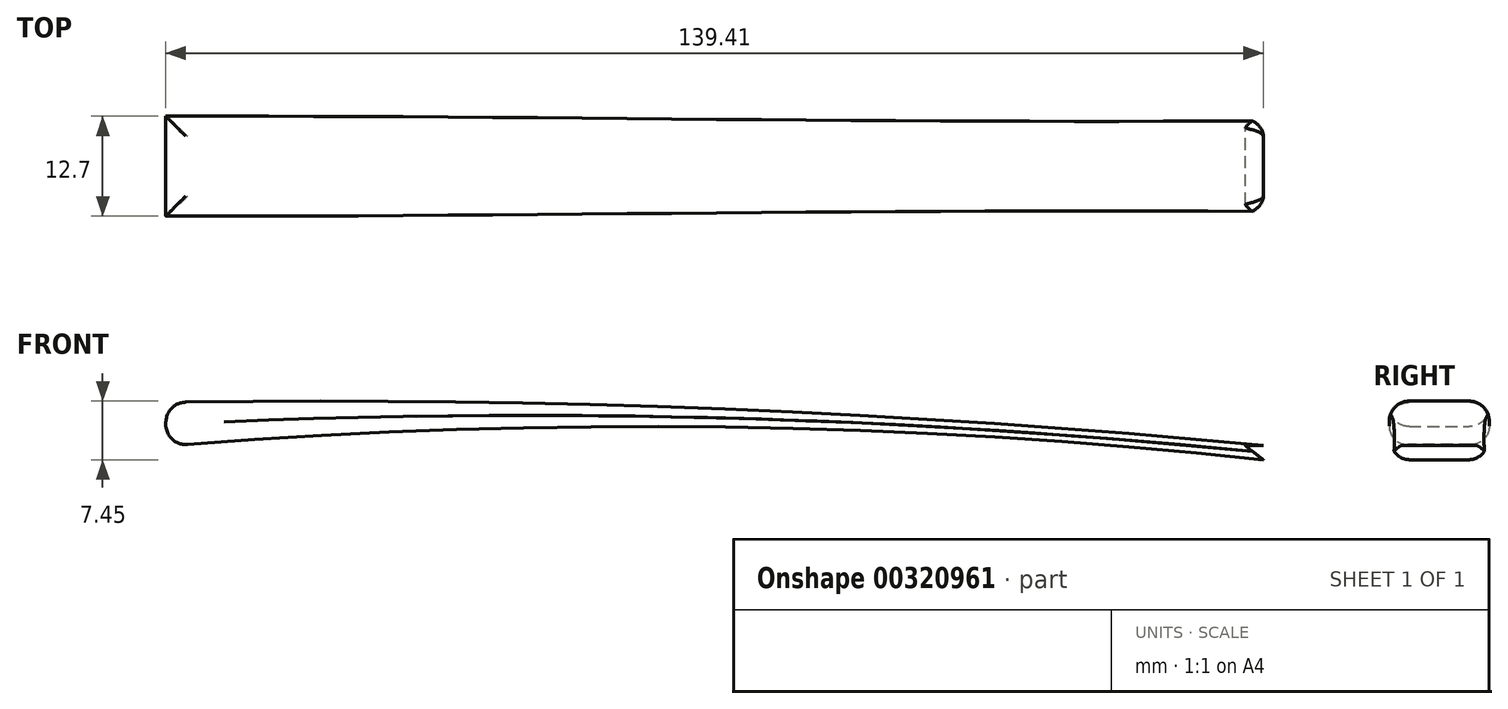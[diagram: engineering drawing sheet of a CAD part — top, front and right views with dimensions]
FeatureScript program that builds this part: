
annotation { "Feature Type Name" : "Feature", "Feature Type Description" : "" }
export const myFeature = defineFeature(function(context is Context, id is Id, definition is map)
    precondition{}
    {
        {
            var Q0;
            Q0=qCreatedBy(makeId("Front.planeOp"),FACE);
            var sketch = newSketch(context, id + "F0", { "sketchPlane" : qUnion([Q0])});
            skLineSegment(sketch, "E0", {"start": v(-25.25, 5.1) * mm, "end": v(13.02, 5.1) * mm});
            skLineSegment(sketch, "E1", {"start": v(13.02, 5.1) * mm, "end": v(13.02, -7.85) * mm});
            skArc(sketch, "E2", {"start": v(-25.25, 5.1) * mm, "mid": v(-7.3, -4.9) * mm, "end": v(13.02, -7.85) * mm});
            skArc(sketch, "E3", {"start": v(-22.97, 5.1) * mm, "mid": v(-92.07, 9.77) * mm, "end": v(-161.33, 10.59) * mm});
            skArc(sketch, "E4", {"start": v(-22.97, 3.3) * mm, "mid": v(-92.1, 7.46) * mm, "end": v(-161.33, 5.1) * mm});
            skArc(sketch, "E5", {"start": v(-161.33, 10.59) * mm, "mid": v(-162.38, 7.84) * mm, "end": v(-161.33, 5.1) * mm});
            skSolve(sketch);
        }
        {
            var Q0;
            {var subQ4=sQuery(id+"F0.wireOp",EDGE,"E3");Q0=makeQuery(id+"F0.imprint","IMPRINT",FACE,{"disambiguationData":[TD([[makeQuery(id+"F0.imprint","IMPRINT",EDGE,{"derivedFrom":subQ4}),1.0]])]});}
            extrude(context, id + "F1", {"entities" : qUnion([Q0]), "endBound" : BoundingType.SYMMETRIC, "depth" : 12.7 * mm});
        }
        {
            var Q0;
            Q0=makeQuery(id+"F1.opExtrude","CAP_EDGE",EDGE,{"disambiguationData":[OSD([sQuery(id+"F0.wireOp",EDGE,"E3")])],"isStart":false});
            var Q1;
            Q1=makeQuery(id+"F1.opExtrude","CAP_EDGE",EDGE,{"disambiguationData":[OSD([sQuery(id+"F0.wireOp",EDGE,"E4")])],"isStart":false});
            var Q2;
            Q2=makeQuery(id+"F1.opExtrude","CAP_EDGE",EDGE,{"disambiguationData":[OSD([sQuery(id+"F0.wireOp",EDGE,"E3")])],"isStart":true});
            var Q3;
            Q3=makeQuery(id+"F1.opExtrude","CAP_EDGE",EDGE,{"disambiguationData":[OSD([sQuery(id+"F0.wireOp",EDGE,"E4")])],"isStart":true});
            var Q4;
            Q4=makeQuery(id+"F1.opExtrude","SWEPT_EDGE",EDGE,{"disambiguationData":[OSD([sQuery(id+"F0.wireOp",EDGE,"E4"),sQuery(id+"F0.wireOp",EDGE,"E5")])]});
            var Q5;
            Q5=makeQuery(id+"F1.opExtrude","SWEPT_EDGE",EDGE,{"disambiguationData":[OSD([sQuery(id+"F0.wireOp",EDGE,"E3"),sQuery(id+"F0.wireOp",EDGE,"E5")])]});
            fillet(context, id + "F2", {"entities" : qUnion([Q0, Q1, Q2, Q3, Q4, Q5]), "radius" : 2.54 * mm, "tangentPropagation" : true, "allowEdgeOverflow" : false});
        }
    });
